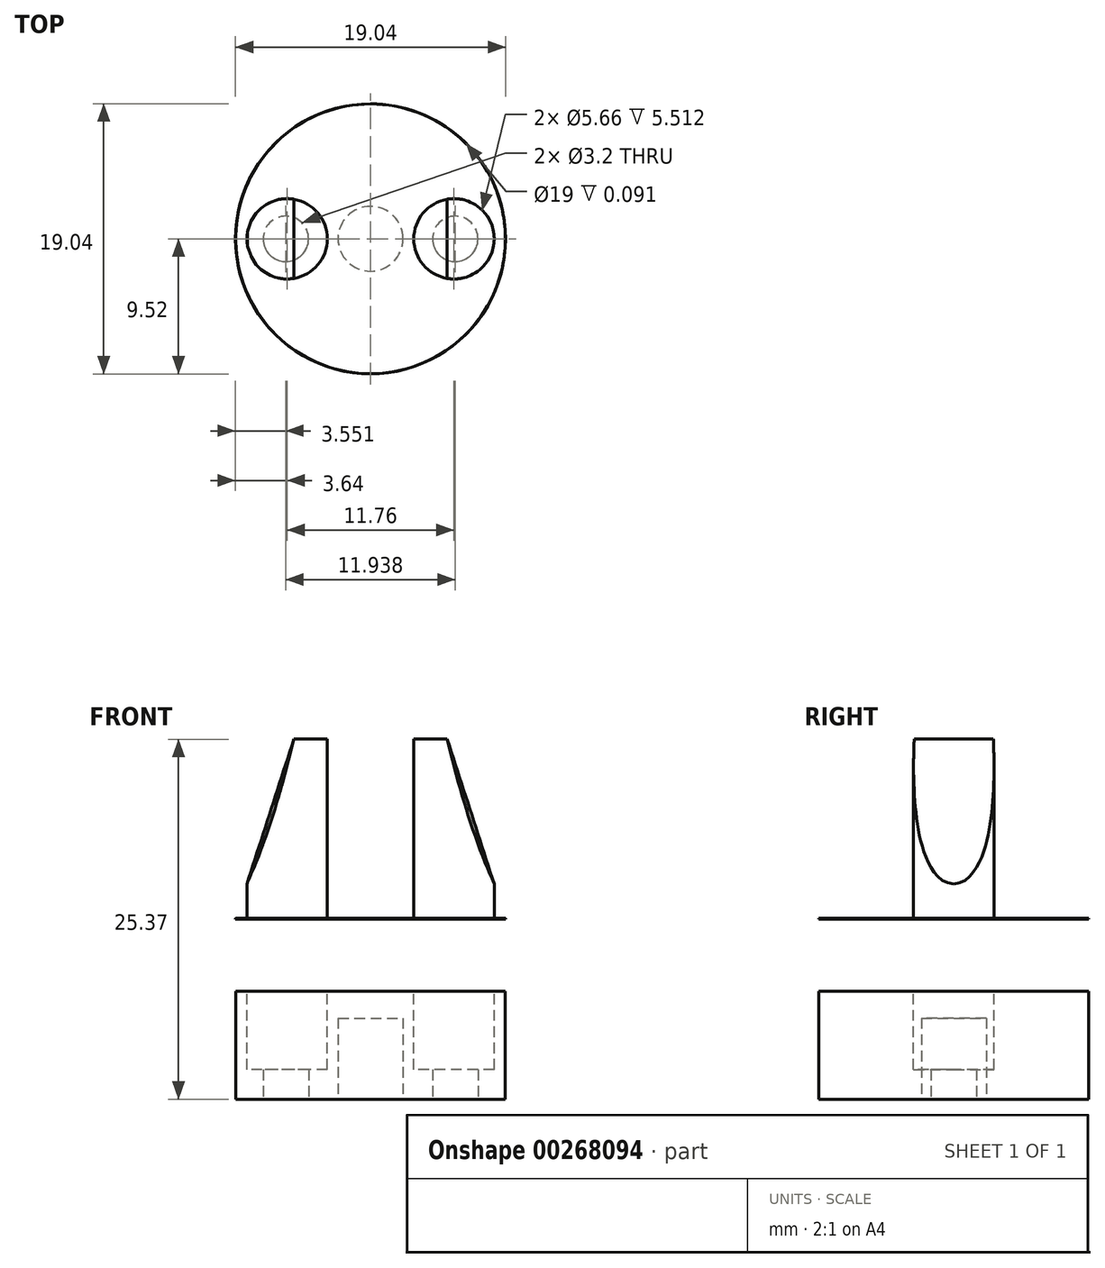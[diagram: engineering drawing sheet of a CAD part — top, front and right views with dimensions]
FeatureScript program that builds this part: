
annotation { "Feature Type Name" : "Feature", "Feature Type Description" : "" }
export const myFeature = defineFeature(function(context is Context, id is Id, definition is map)
    precondition{}
    {
        {
            var Q0;
            Q0=qCreatedBy(makeId("Top.planeOp"),FACE);
            var sketch = newSketch(context, id + "F0", { "sketchPlane" : qUnion([Q0])});
            skCircle(sketch, "E0", {"center": v(0, 0) * mm, "radius": 9.5 * mm});
            skSolve(sketch);
        }
        {
            var Q0;
            Q0 = qSketchRegion(id + "F0", true);
            extrude(context, id + "F1", {"entities" : qUnion([Q0]), "depth" : 5.46 * mm});
        }
        {
            var Q0;
            Q0=makeQuery(id+"F1.opExtrude","CAP_FACE",FACE,{"disambiguationData":[OSD([sQuery(id+"F0.wireOp",EDGE,"E0")])],"isStart":true});
            var sketch = newSketch(context, id + "F2", { "sketchPlane" : qUnion([Q0])});
            skCircle(sketch, "E1", {"center": v(0, 0) * mm, "radius": 2.29 * mm});
            skSolve(sketch);
        }
        {
            var Q0;
            Q0=makeQuery(id+"F1.opExtrude","CAP_FACE",FACE,{"disambiguationData":[OSD([sQuery(id+"F0.wireOp",EDGE,"E0")])],"isStart":false});
            var sketch = newSketch(context, id + "F3", { "sketchPlane" : qUnion([Q0])});
            skLineSegment(sketch, "E2", {"start": v(40.48, 0) * mm, "end": v(-36.27, 0) * mm});
            skLineSegment(sketch, "E3", {"start": v(0, -32.93) * mm, "end": v(0, 30.65) * mm});
            skCircle(sketch, "E4", {"center": v(-5.88, 0) * mm, "radius": 2.83 * mm});
            skCircle(sketch, "E5", {"center": v(5.88, 0) * mm, "radius": 2.83 * mm});
            skSolve(sketch);
        }
        {
            var Q0;
            Q0 = qSketchRegion(id + "F3", true);
            extrude(context, id + "F4", {"entities" : qUnion([Q0]), "operationType" : NewBodyOperationType.REMOVE, "oppositeDirection" : true, "depth" : 3.38 * mm, "hasSecondDirection" : true, "secondDirectionOppositeDirection" : false, "secondDirectionDepth" : 127 * mm});
        }
        {
            var Q0;
            Q0=makeQuery(id+"F1.opExtrude","CAP_FACE",FACE,{"disambiguationData":[OSD([sQuery(id+"F0.wireOp",EDGE,"E0")])],"isStart":false});
            extrude(context, id + "F5", {"entities" : qUnion([Q0]), "operationType" : NewBodyOperationType.ADD, "depth" : 7.2 * mm});
        }
        {
            var Q0;
            Q0=makeQuery(id+"F2.imprint","IMPRINT",FACE,{"disambiguationData":[TD([[makeQuery(id+"F2.imprint","IMPRINT",EDGE,{"derivedFrom":sQuery(id+"F2.wireOp",EDGE,"E1")}),1.0]])]});
            extrude(context, id + "F6", {"entities" : qUnion([Q0]), "operationType" : NewBodyOperationType.REMOVE, "oppositeDirection" : true, "depth" : 5.7 * mm});
        }
        {
            var Q0;
            Q0=makeQuery(id+"F1.opExtrude","CAP_FACE",FACE,{"disambiguationData":[OSD([sQuery(id+"F0.wireOp",EDGE,"E0")])],"isStart":true});
            var sketch = newSketch(context, id + "F7", { "sketchPlane" : qUnion([Q0])});
            skLineSegment(sketch, "E6", {"start": v(0, 11.13) * mm, "end": v(0, -12.12) * mm});
            skLineSegment(sketch, "E7", {"start": v(-13.9, 0) * mm, "end": v(12.77, 0) * mm});
            skCircle(sketch, "E8", {"center": v(5.97, 0) * mm, "radius": 1.6 * mm});
            skCircle(sketch, "E9", {"center": v(-5.97, 0) * mm, "radius": 1.6 * mm});
            skSolve(sketch);
        }
        {
            var Q0;
            Q0 = qSketchRegion(id + "F7", true);
            extrude(context, id + "F8", {"entities" : qUnion([Q0]), "operationType" : NewBodyOperationType.REMOVE, "oppositeDirection" : true, "depth" : 127 * mm});
        }
        {
            var Q0;
            Q0=makeQuery(id+"F5.opExtrude","CAP_FACE",FACE,{"disambiguationData":[OSD([sQuery(id+"F0.wireOp",EDGE,"E0")])],"isStart":false});
            cPlane(context, id + "F9", {"entities" : qUnion([Q0]), "cplaneType" : CPlaneType.OFFSET, "offset" : 12.7 * mm, "width" : 152.4 * mm, "height" : 152.4 * mm});
        }
        {
            var Q0;
            Q0=qCreatedBy(id+"F9.planeOp",FACE);
            var sketch = newSketch(context, id + "F10", { "sketchPlane" : qUnion([Q0])});
            skCircle(sketch, "E10.cCircle", {"center": v(0, 0) * mm, "radius": 6.23 * mm, "construction": true});
            skLineSegment(sketch, "E10.0", {"start": v(0, -6.23) * mm, "end": v(-5.4, -3.12) * mm});
            skLineSegment(sketch, "E10.1", {"start": v(-5.4, -3.12) * mm, "end": v(-5.4, 3.12) * mm});
            skLineSegment(sketch, "E10.2", {"start": v(-5.4, 3.12) * mm, "end": v(0, 6.23) * mm});
            skLineSegment(sketch, "E10.3", {"start": v(0, 6.23) * mm, "end": v(5.4, 3.12) * mm});
            skLineSegment(sketch, "E10.4", {"start": v(5.4, 3.12) * mm, "end": v(5.4, -3.12) * mm});
            skLineSegment(sketch, "E10.5", {"start": v(5.4, -3.12) * mm, "end": v(0, -6.23) * mm});
            skSolve(sketch);
        }
        {
            var Q0;
            Q0=makeQuery(id+"F5.opExtrude","CAP_FACE",FACE,{"disambiguationData":[OSD([sQuery(id+"F0.wireOp",EDGE,"E0")])],"isStart":false});
            var sketch = newSketch(context, id + "F11", { "sketchPlane" : qUnion([Q0])});
            skCircle(sketch, "E11", {"center": v(0, 0) * mm, "radius": 9.52 * mm});
            skSolve(sketch);
        }
        {
            var Q0;
            Q0 = qSketchRegion(id + "F11", true);
            extrude(context, id + "F12", {"entities" : qUnion([Q0]), "operationType" : NewBodyOperationType.ADD, "depth" : 0.03 * mm});
        }
        {
            var Q1;
            Q1=makeQuery(id+"F10.imprint","IMPRINT",FACE,{"disambiguationData":[TD([[makeQuery(id+"F10.imprint","IMPRINT",EDGE,{"derivedFrom":sQuery(id+"F10.wireOp",EDGE,"E10.0")}),-1.0]])]});
            var Q2;
            Q2=makeQuery(id+"F12.opExtrude","CAP_FACE",FACE,{"disambiguationData":[OSD([sQuery(id+"F11.wireOp",EDGE,"E11")])],"isStart":false});
            loft(context, id + "F13", {"operationType" : NewBodyOperationType.ADD, "sheetProfilesArray" : [{ "sheetProfileEntities" : qUnion([Q1]) }, { "sheetProfileEntities" : qUnion([Q2]) }]});
        }
        {
            var Q0;
            Q0=makeQuery(id+"F13.opLoft","CAP_FACE",FACE,{"disambiguationData":[OSD([makeQuery(id+"F10.imprint","IMPRINT",FACE,{"disambiguationData":[TD([[makeQuery(id+"F10.imprint","IMPRINT",EDGE,{"derivedFrom":sQuery(id+"F10.wireOp",EDGE,"E10.0")}),-1.0]])]})])],"isStart":true});
            var sketch = newSketch(context, id + "F14", { "sketchPlane" : qUnion([Q0])});
            skLineSegment(sketch, "E12.bottom", {"start": v(-1.9, -1.9) * mm, "end": v(1.9, -1.9) * mm});
            skLineSegment(sketch, "E12.top", {"start": v(-1.9, 1.9) * mm, "end": v(1.9, 1.9) * mm});
            skLineSegment(sketch, "E12.left", {"start": v(-1.9, -1.9) * mm, "end": v(-1.9, 1.9) * mm});
            skLineSegment(sketch, "E12.right", {"start": v(1.9, -1.9) * mm, "end": v(1.9, 1.9) * mm});
            skPoint(sketch, "E12.middle", {"position": v(0, 0) * mm});
            skSolve(sketch);
        }
        {
            var Q0;
            Q0 = qSketchRegion(id + "F14", true);
            extrude(context, id + "F15", {"entities" : qUnion([Q0]), "operationType" : NewBodyOperationType.REMOVE, "oppositeDirection" : true, "depth" : 17.78 * mm});
        }
        {
            var Q0;
            Q0=makeQuery(id+"F13.opLoft","CAP_FACE",FACE,{"disambiguationData":[OSD([makeQuery(id+"F10.imprint","IMPRINT",FACE,{"disambiguationData":[TD([[makeQuery(id+"F10.imprint","IMPRINT",EDGE,{"derivedFrom":sQuery(id+"F10.wireOp",EDGE,"E10.0")}),-1.0]])]})])],"isStart":true});
            var sketch = newSketch(context, id + "F16", { "sketchPlane" : qUnion([Q0])});
            skLineSegment(sketch, "E13", {"start": v(17.23, 0) * mm, "end": v(-19.92, 0) * mm});
            skLineSegment(sketch, "E14", {"start": v(0, -17.96) * mm, "end": v(0, 15.98) * mm});
            skCircle(sketch, "E15", {"center": v(-5.88, 0) * mm, "radius": 2.83 * mm});
            skCircle(sketch, "E16", {"center": v(5.88, 0) * mm, "radius": 2.83 * mm});
            skCircle(sketch, "E17", {"center": v(0, 0) * mm, "radius": 9.5 * mm});
            skSolve(sketch);
        }
        {
            var Q0;
            {var subQ0=sQuery(id+"F16.wireOp",EDGE,"E16");var subQ1=sQuery(id+"F16.wireOp",EDGE,"E13");var subQ2=makeQuery(id+"F16.imprint","INTERSECT",VERTEX,{"disambiguationData":[OD(1.0)],"derivedFrom":[subQ1,subQ0]});Q0=makeQuery(id+"F16.imprint","IMPRINT",FACE,{"disambiguationData":[TD([[makeQuery(id+"F16.imprint","IMPRINT",EDGE,{"disambiguationData":[TD([[subQ2,1.0]])],"derivedFrom":subQ1}),1.0]])]});}
            var Q1;
            {var subQ0=sQuery(id+"F16.wireOp",EDGE,"E16");var subQ1=sQuery(id+"F16.wireOp",EDGE,"E13");var subQ2=makeQuery(id+"F16.imprint","INTERSECT",VERTEX,{"disambiguationData":[OD(0.0)],"derivedFrom":[subQ1,subQ0]});Q1=makeQuery(id+"F16.imprint","IMPRINT",FACE,{"disambiguationData":[TD([[makeQuery(id+"F16.imprint","IMPRINT",EDGE,{"disambiguationData":[TD([[subQ2,-1.0]])],"derivedFrom":subQ1}),1.0]])]});}
            var Q2;
            {var subQ0=sQuery(id+"F16.wireOp",EDGE,"E16");var subQ1=sQuery(id+"F16.wireOp",EDGE,"E13");var subQ2=makeQuery(id+"F16.imprint","INTERSECT",VERTEX,{"disambiguationData":[OD(0.0)],"derivedFrom":[subQ1,subQ0]});Q2=makeQuery(id+"F16.imprint","IMPRINT",FACE,{"disambiguationData":[TD([[makeQuery(id+"F16.imprint","IMPRINT",EDGE,{"disambiguationData":[TD([[subQ2,-1.0]])],"derivedFrom":subQ1}),-1.0]])]});}
            var Q3;
            {var subQ0=sQuery(id+"F16.wireOp",EDGE,"E16");var subQ1=sQuery(id+"F16.wireOp",EDGE,"E13");var subQ2=makeQuery(id+"F16.imprint","INTERSECT",VERTEX,{"disambiguationData":[OD(1.0)],"derivedFrom":[subQ1,subQ0]});Q3=makeQuery(id+"F16.imprint","IMPRINT",FACE,{"disambiguationData":[TD([[makeQuery(id+"F16.imprint","IMPRINT",EDGE,{"disambiguationData":[TD([[subQ2,1.0]])],"derivedFrom":subQ1}),-1.0]])]});}
            var Q4;
            {var subQ0=sQuery(id+"F16.wireOp",EDGE,"E15");var subQ1=sQuery(id+"F16.wireOp",EDGE,"E13");var subQ2=makeQuery(id+"F16.imprint","INTERSECT",VERTEX,{"disambiguationData":[OD(0.0)],"derivedFrom":[subQ1,subQ0]});Q4=makeQuery(id+"F16.imprint","IMPRINT",FACE,{"disambiguationData":[TD([[makeQuery(id+"F16.imprint","IMPRINT",EDGE,{"disambiguationData":[TD([[subQ2,1.0]])],"derivedFrom":subQ1}),1.0]])]});}
            var Q5;
            {var subQ0=sQuery(id+"F16.wireOp",EDGE,"E15");var subQ1=sQuery(id+"F16.wireOp",EDGE,"E13");var subQ2=makeQuery(id+"F16.imprint","INTERSECT",VERTEX,{"disambiguationData":[OD(1.0)],"derivedFrom":[subQ1,subQ0]});Q5=makeQuery(id+"F16.imprint","IMPRINT",FACE,{"disambiguationData":[TD([[makeQuery(id+"F16.imprint","IMPRINT",EDGE,{"disambiguationData":[TD([[subQ2,-1.0]])],"derivedFrom":subQ1}),1.0]])]});}
            var Q6;
            {var subQ0=sQuery(id+"F16.wireOp",EDGE,"E15");var subQ1=sQuery(id+"F16.wireOp",EDGE,"E13");var subQ2=makeQuery(id+"F16.imprint","INTERSECT",VERTEX,{"disambiguationData":[OD(0.0)],"derivedFrom":[subQ1,subQ0]});Q6=makeQuery(id+"F16.imprint","IMPRINT",FACE,{"disambiguationData":[TD([[makeQuery(id+"F16.imprint","IMPRINT",EDGE,{"disambiguationData":[TD([[subQ2,1.0]])],"derivedFrom":subQ1}),-1.0]])]});}
            var Q7;
            {var subQ0=sQuery(id+"F16.wireOp",EDGE,"E15");var subQ1=sQuery(id+"F16.wireOp",EDGE,"E13");var subQ2=makeQuery(id+"F16.imprint","INTERSECT",VERTEX,{"disambiguationData":[OD(1.0)],"derivedFrom":[subQ1,subQ0]});Q7=makeQuery(id+"F16.imprint","IMPRINT",FACE,{"disambiguationData":[TD([[makeQuery(id+"F16.imprint","IMPRINT",EDGE,{"disambiguationData":[TD([[subQ2,-1.0]])],"derivedFrom":subQ1}),-1.0]])]});}
            extrude(context, id + "F17", {"entities" : qUnion([Q0, Q1, Q2, Q3, Q4, Q5, Q6, Q7]), "operationType" : NewBodyOperationType.REMOVE, "oppositeDirection" : true, "depth" : 17.78 * mm});
        }
    });
